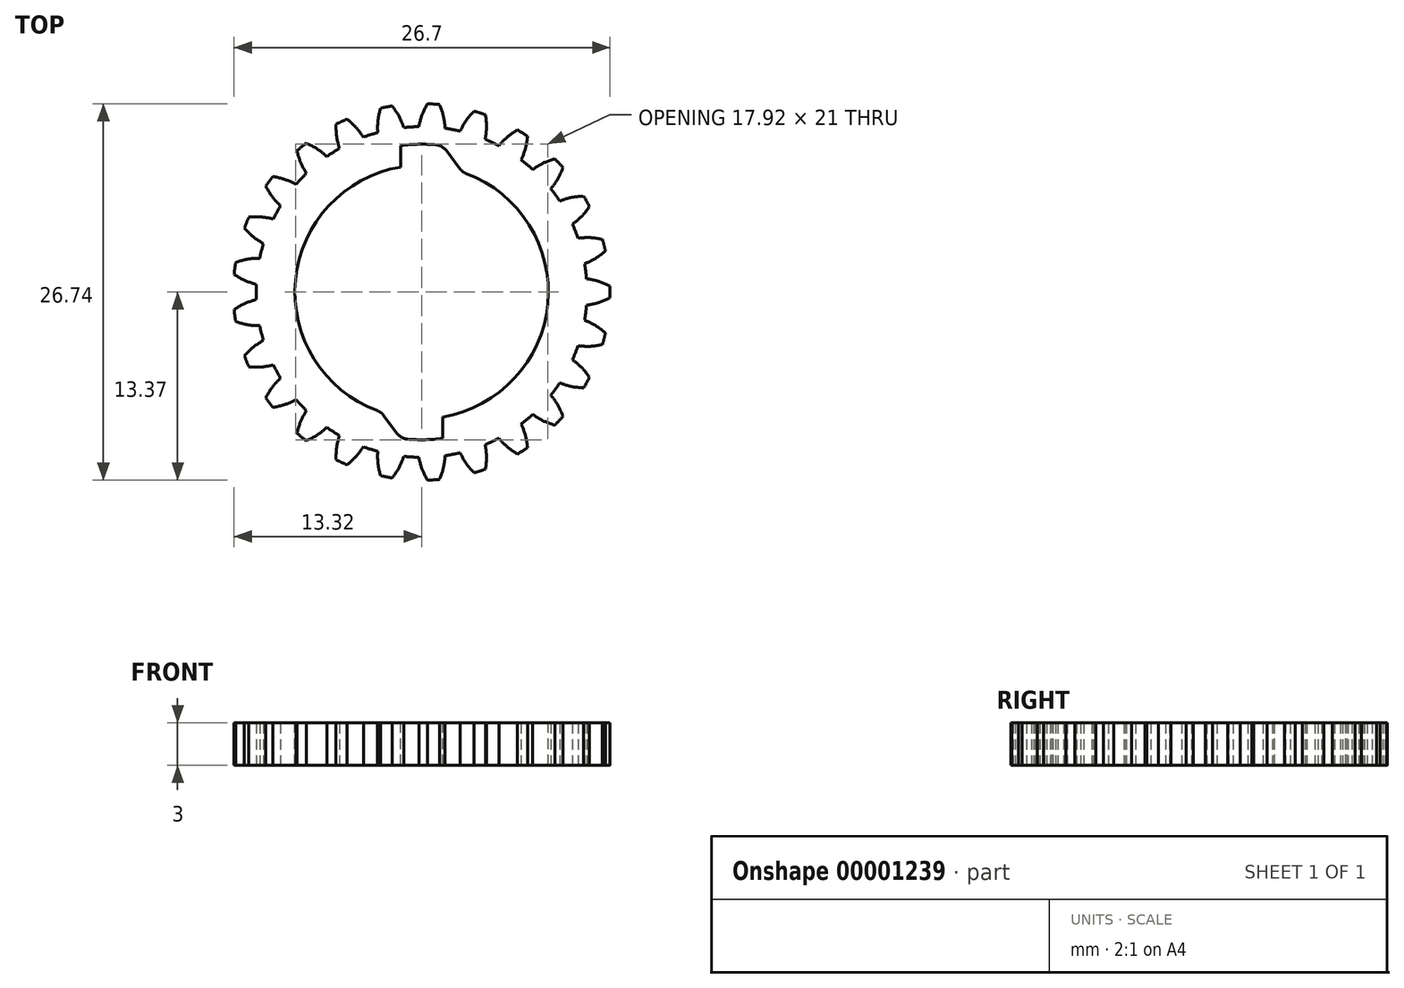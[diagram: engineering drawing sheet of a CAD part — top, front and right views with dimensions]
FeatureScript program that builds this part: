
annotation { "Feature Type Name" : "Feature", "Feature Type Description" : "" }
export const myFeature = defineFeature(function(context is Context, id is Id, definition is map)
    precondition{}
    {
        {
            var Q0;
            Q0=qCreatedBy(makeId("Top.planeOp"),FACE);
            var sketch = newSketch(context, id + "F0", { "sketchPlane" : qUnion([Q0])});
            skCircle(sketch, "E0", {"center": v(0, 0) * mm, "radius": 12.5 * mm, "construction": true});
            skLineSegment(sketch, "E1", {"start": v(0, 0) * mm, "end": v(0, 9.18) * mm, "construction": true});
            skLineSegment(sketch, "E2", {"start": v(6.37, 12.5) * mm, "end": v(-7.67, 12.5) * mm, "construction": true});
            skLineSegment(sketch, "E3", {"start": v(0, 12.5) * mm, "end": v(8.24, 9.5) * mm, "construction": true});
            skLineSegment(sketch, "E4", {"start": v(0, 0) * mm, "end": v(4.02, 11.04) * mm, "construction": true});
            skCircle(sketch, "E5", {"center": v(0, 0) * mm, "radius": 11.75 * mm, "construction": true});
            skArc(sketch, "E6", {"start": v(4.02, 11.04) * mm, "mid": v(4.94, 10.66) * mm, "end": v(5.83, 10.2) * mm, "construction": true});
            skLineSegment(sketch, "E7", {"start": v(0, 0) * mm, "end": v(5.83, 10.2) * mm, "construction": true});
            skLineSegment(sketch, "E8", {"start": v(5.83, 10.2) * mm, "end": v(0.38, 13.31) * mm, "construction": true});
            skArc(sketch, "E9", {"start": v(4.02, 11.04) * mm, "mid": v(3.3, 11.27) * mm, "end": v(2.58, 11.46) * mm, "construction": true});
            skLineSegment(sketch, "E10", {"start": v(0, 0) * mm, "end": v(2.58, 11.46) * mm, "construction": true});
            skLineSegment(sketch, "E11", {"start": v(2.58, 11.46) * mm, "end": v(-0.13, 12.07) * mm, "construction": true});
            skArc(sketch, "E12", {"start": v(4.02, 11.04) * mm, "mid": v(4.48, 10.86) * mm, "end": v(4.94, 10.66) * mm});
            skLineSegment(sketch, "E13", {"start": v(4.94, 10.66) * mm, "end": v(0, 0) * mm, "construction": true});
            skLineSegment(sketch, "E14", {"start": v(4.94, 10.66) * mm, "end": v(0.16, 12.88) * mm, "construction": true});
            skArc(sketch, "E15", {"start": v(4.02, 11.04) * mm, "mid": v(5.08, 10.6) * mm, "end": v(6.09, 10.05) * mm});
            skLineSegment(sketch, "E16", {"start": v(0, 0) * mm, "end": v(6.09, 10.05) * mm, "construction": true});
            skLineSegment(sketch, "E17", {"start": v(6.09, 10.05) * mm, "end": v(0.47, 13.45) * mm, "construction": true});
            skSolve(sketch);
        }
        {
            var Q0;
            Q0=qCreatedBy(makeId("Top.planeOp"),FACE);
            var sketch = newSketch(context, id + "F1", { "sketchPlane" : qUnion([Q0])});
            skPoint(sketch, "E18.0", {"position": v(0.38, 13.31) * mm});
            skPoint(sketch, "E19.0", {"position": v(0.16, 12.88) * mm});
            skPoint(sketch, "E20.0", {"position": v(0, 12.5) * mm});
            skPoint(sketch, "E21.0", {"position": v(-0.13, 12.07) * mm});
            skCircle(sketch, "E22.0", {"center": v(0, 0) * mm, "radius": 11.75 * mm, "construction": true});
            skLineSegment(sketch, "E23", {"start": v(0, 0) * mm, "end": v(0.74, 11.72) * mm, "construction": true});
            skPoint(sketch, "E24.0", {"position": v(0.47, 13.45) * mm});
            skFitSpline(sketch, "E25", {"points": [v(0.47, 13.45) * mm, v(0.38, 13.31) * mm, v(0.16, 12.88) * mm, v(0, 12.5) * mm, v(-0.13, 12.07) * mm, v(-0.2, 11.74) * mm], "startDerivative": vector(-0.53, -0.87) * mm, "endDerivative": vector(-0.32, -1.63) * mm});
            skPoint(sketch, "E26.MirrorP", {"position": v(1.22, 13.4) * mm});
            skPoint(sketch, "E27.MirrorP", {"position": v(1.64, 11.96) * mm});
            skFitSpline(sketch, "E28.MirrorCS", {"points": [v(1.22, 13.4) * mm, v(1.29, 13.25) * mm, v(1.46, 12.8) * mm, v(1.57, 12.4) * mm, v(1.64, 11.96) * mm, v(1.67, 11.63) * mm], "startDerivative": vector(0.42, -0.93) * mm, "endDerivative": vector(0.11, -1.66) * mm});
            skArc(sketch, "E29", {"start": v(-0.2, 11.74) * mm, "mid": v(-0.74, -11.72) * mm, "end": v(1.67, 11.63) * mm});
            skCircle(sketch, "E30", {"center": v(0, 0) * mm, "radius": 13.38 * mm});
            skSolve(sketch);
        }
        {
            var Q0;
            Q0=makeQuery(id+"F1.imprint","IMPRINT",FACE,{"disambiguationData":[TD([[makeQuery(id+"F1.imprint","IMPRINT",EDGE,{"derivedFrom":sQuery(id+"F1.wireOp",EDGE,"E25")}),1.0]])]});
            extrude(context, id + "F2", {"entities" : qUnion([Q0]), "depth" : 3 * mm});
        }
        {
            var Q0;
            Q0=qCreatedBy(makeId("Front.planeOp"),FACE);
            var sketch = newSketch(context, id + "F3", { "sketchPlane" : qUnion([Q0])});
            skLineSegment(sketch, "E31", {"start": v(0, 0) * mm, "end": v(0, 2.97) * mm, "construction": true});
            skSolve(sketch);
        }
        {
            var Q0;
            Q0=makeQuery(id+"F2.opExtrude","SWEPT_BODY",BODY,{"disambiguationData":[OSD([sQuery(id+"F1.wireOp",EDGE,"E25"),sQuery(id+"F1.wireOp",EDGE,"E28.MirrorCS"),sQuery(id+"F1.wireOp",EDGE,"E29"),sQuery(id+"F1.wireOp",EDGE,"b7b7ef6c-d85d-42a2-9839-c4a0e2017a31")])]});
            var Q1;
            Q1=sQuery(id+"F3.wireOp",EDGE,"E31");
            circularPattern(context, id + "F4", {"operationType" : NewBodyOperationType.ADD, "entities" : qUnion([Q0]), "axis" : qUnion([Q1]), "angle" : 360 * degree, "instanceCount" : 25, "equalSpace" : true});
        }
        {
            var Q0;
            {var subQ0=makeQuery(id+"F2.opExtrude","CAP_FACE",FACE,{"disambiguationData":[OSD([sQuery(id+"F1.wireOp",EDGE,"E25"),sQuery(id+"F1.wireOp",EDGE,"E28.MirrorCS"),sQuery(id+"F1.wireOp",EDGE,"E29"),sQuery(id+"F1.wireOp",EDGE,"E30")])],"isStart":false});Q0=makeQuery(id+"F4.boolean.opBoolean","MERGE",FACE,{"derivedFrom":[subQ0,makeQuery(id+"F4.opPattern","COPY",FACE,{"derivedFrom":subQ0,"instanceName":"1"}),makeQuery(id+"F4.opPattern","COPY",FACE,{"derivedFrom":subQ0,"instanceName":"2"}),makeQuery(id+"F4.opPattern","COPY",FACE,{"derivedFrom":subQ0,"instanceName":"3"}),makeQuery(id+"F4.opPattern","COPY",FACE,{"derivedFrom":subQ0,"instanceName":"4"}),makeQuery(id+"F4.opPattern","COPY",FACE,{"derivedFrom":subQ0,"instanceName":"5"}),makeQuery(id+"F4.opPattern","COPY",FACE,{"derivedFrom":subQ0,"instanceName":"6"}),makeQuery(id+"F4.opPattern","COPY",FACE,{"derivedFrom":subQ0,"instanceName":"7"}),makeQuery(id+"F4.opPattern","COPY",FACE,{"derivedFrom":subQ0,"instanceName":"8"}),makeQuery(id+"F4.opPattern","COPY",FACE,{"derivedFrom":subQ0,"instanceName":"9"}),makeQuery(id+"F4.opPattern","COPY",FACE,{"derivedFrom":subQ0,"instanceName":"10"}),makeQuery(id+"F4.opPattern","COPY",FACE,{"derivedFrom":subQ0,"instanceName":"11"}),makeQuery(id+"F4.opPattern","COPY",FACE,{"derivedFrom":subQ0,"instanceName":"12"}),makeQuery(id+"F4.opPattern","COPY",FACE,{"derivedFrom":subQ0,"instanceName":"13"}),makeQuery(id+"F4.opPattern","COPY",FACE,{"derivedFrom":subQ0,"instanceName":"14"}),makeQuery(id+"F4.opPattern","COPY",FACE,{"derivedFrom":subQ0,"instanceName":"15"}),makeQuery(id+"F4.opPattern","COPY",FACE,{"derivedFrom":subQ0,"instanceName":"16"}),makeQuery(id+"F4.opPattern","COPY",FACE,{"derivedFrom":subQ0,"instanceName":"17"}),makeQuery(id+"F4.opPattern","COPY",FACE,{"derivedFrom":subQ0,"instanceName":"18"}),makeQuery(id+"F4.opPattern","COPY",FACE,{"derivedFrom":subQ0,"instanceName":"19"}),makeQuery(id+"F4.opPattern","COPY",FACE,{"derivedFrom":subQ0,"instanceName":"20"}),makeQuery(id+"F4.opPattern","COPY",FACE,{"derivedFrom":subQ0,"instanceName":"21"}),makeQuery(id+"F4.opPattern","COPY",FACE,{"derivedFrom":subQ0,"instanceName":"22"}),makeQuery(id+"F4.opPattern","COPY",FACE,{"derivedFrom":subQ0,"instanceName":"23"}),makeQuery(id+"F4.opPattern","COPY",FACE,{"derivedFrom":subQ0,"instanceName":"24"})]});}
            var sketch = newSketch(context, id + "F5", { "sketchPlane" : qUnion([Q0])});
            skArc(sketch, "E32", {"start": v(-1.5, 8.87) * mm, "mid": v(-8.97, 0.72) * mm, "end": v(-2.9, -8.52) * mm});
            skCircle(sketch, "E33", {"center": v(0, 0) * mm, "radius": 10.5 * mm, "construction": true});
            skArc(sketch, "E34", {"start": v(-1.5, 10.4) * mm, "mid": v(0, 10.5) * mm, "end": v(1.49, 10.4) * mm});
            skLineSegment(sketch, "E35", {"start": v(1.49, 10.4) * mm, "end": v(2.9, 8.52) * mm});
            skLineSegment(sketch, "E36", {"start": v(1.49, 10.4) * mm, "end": v(6.17, 9.72) * mm, "construction": true});
            skArc(sketch, "E37", {"start": v(1.5, -10.4) * mm, "mid": v(0, -10.5) * mm, "end": v(-1.49, -10.4) * mm});
            skLineSegment(sketch, "E38", {"start": v(-1.49, -10.4) * mm, "end": v(-2.9, -8.52) * mm});
            skArc(sketch, "E39.trimOffspring", {"start": v(1.5, -8.87) * mm, "mid": v(8.97, -0.72) * mm, "end": v(2.9, 8.52) * mm});
            skLineSegment(sketch, "E40", {"start": v(-1.49, -10.4) * mm, "end": v(-6.7, -9.65) * mm, "construction": true});
            skLineSegment(sketch, "E41", {"start": v(-1.5, 8.87) * mm, "end": v(-1.5, 10.4) * mm});
            skLineSegment(sketch, "E42", {"start": v(1.5, -8.87) * mm, "end": v(1.5, -10.4) * mm});
            skSolve(sketch);
        }
        {
            var Q0;
            Q0=makeQuery(id+"F5.imprint","IMPRINT",FACE,{"disambiguationData":[TD([[makeQuery(id+"F5.imprint","IMPRINT",EDGE,{"derivedFrom":sQuery(id+"F5.wireOp",EDGE,"E32")}),1.0]])]});
            extrude(context, id + "F6", {"entities" : qUnion([Q0]), "operationType" : NewBodyOperationType.REMOVE, "endBound" : BoundingType.UP_TO_NEXT, "oppositeDirection" : true, "depth" : 25 * mm});
        }
        {
            var Q0;
            Q0=makeQuery(id+"F6.boolean.opBoolean","COPY",EDGE,{"derivedFrom":makeQuery(id+"F6.opExtrude","SWEPT_EDGE",EDGE,{"disambiguationData":[OSD([sQuery(id+"F5.wireOp",EDGE,"E37"),sQuery(id+"F5.wireOp",EDGE,"E38")])]})});
            var Q1;
            Q1=makeQuery(id+"F6.boolean.opBoolean","COPY",EDGE,{"derivedFrom":makeQuery(id+"F6.opExtrude","SWEPT_EDGE",EDGE,{"disambiguationData":[OSD([sQuery(id+"F5.wireOp",EDGE,"E34"),sQuery(id+"F5.wireOp",EDGE,"E35")])]})});
            var Q2;
            Q2=makeQuery(id+"F6.boolean.opBoolean","COPY",EDGE,{"derivedFrom":makeQuery(id+"F6.opExtrude","SWEPT_EDGE",EDGE,{"disambiguationData":[OSD([sQuery(id+"F5.wireOp",EDGE,"E35"),sQuery(id+"F5.wireOp",EDGE,"E39.trimOffspring")])]})});
            var Q3;
            Q3=makeQuery(id+"F6.boolean.opBoolean","COPY",EDGE,{"derivedFrom":makeQuery(id+"F6.opExtrude","SWEPT_EDGE",EDGE,{"disambiguationData":[OSD([sQuery(id+"F5.wireOp",EDGE,"E32"),sQuery(id+"F5.wireOp",EDGE,"E38")])]})});
            fillet(context, id + "F7", {"entities" : qUnion([Q0, Q1, Q2, Q3]), "radius" : 1 * mm, "tangentPropagation" : true, "allowEdgeOverflow" : false});
        }
    });
